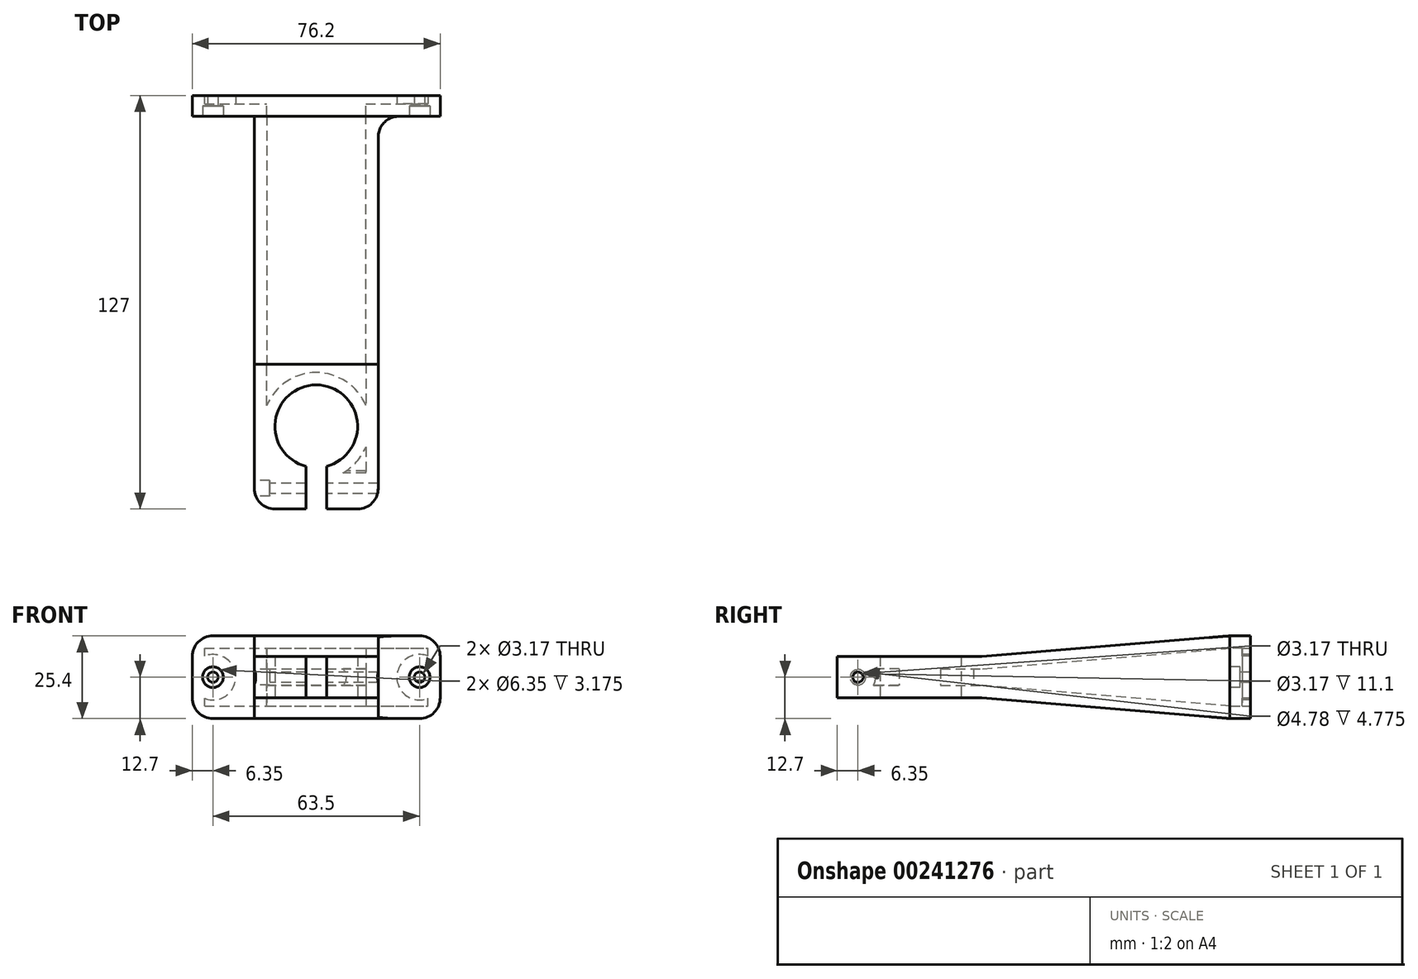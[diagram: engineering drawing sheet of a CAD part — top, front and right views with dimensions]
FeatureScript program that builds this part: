
annotation { "Feature Type Name" : "Feature", "Feature Type Description" : "" }
export const myFeature = defineFeature(function(context is Context, id is Id, definition is map)
    precondition{}
    {
        {
            var Q0;
            Q0=qCreatedBy(makeId("Front.planeOp"),FACE);
            var sketch = newSketch(context, id + "F0", { "sketchPlane" : qUnion([Q0])});
            skLineSegment(sketch, "E0.bottom", {"start": v(0, 0) * mm, "end": v(76.2, 0) * mm});
            skLineSegment(sketch, "E0.top", {"start": v(0, 25.4) * mm, "end": v(76.2, 25.4) * mm});
            skLineSegment(sketch, "E0.left", {"start": v(0, 0) * mm, "end": v(0, 25.4) * mm});
            skLineSegment(sketch, "E0.right", {"start": v(76.2, 0) * mm, "end": v(76.2, 25.4) * mm});
            skSolve(sketch);
        }
        {
            var Q0;
            Q0 = qSketchRegion(id + "F0", true);
            extrude(context, id + "F1", {"entities" : qUnion([Q0]), "depth" : 6.35 * mm});
        }
        {
            var Q0;
            Q0=makeQuery(id+"F1.opExtrude","CAP_FACE",FACE,{"disambiguationData":[OSD([sQuery(id+"F0.wireOp",EDGE,"E0.bottom"),sQuery(id+"F0.wireOp",EDGE,"E0.top"),sQuery(id+"F0.wireOp",EDGE,"E0.left"),sQuery(id+"F0.wireOp",EDGE,"E0.right")])],"isStart":false});
            var sketch = newSketch(context, id + "F2", { "sketchPlane" : qUnion([Q0])});
            skPoint(sketch, "E1", {"position": v(6.35, 12.7) * mm});
            skPoint(sketch, "E1.positionSnap0", {"position": v(0, 12.7) * mm});
            skPoint(sketch, "E2", {"position": v(69.85, 12.7) * mm});
            skSolve(sketch);
        }
        {
            var Q0;
            Q0=sQuery(id+"F2.wireOp",VERTEX,"E1");
            var Q1;
            Q1=sQuery(id+"F2.wireOp",VERTEX,"E2");
            var Q2;
            Q2=makeQuery(id+"F1.opExtrude","SWEPT_BODY",BODY,{"disambiguationData":[OSD([sQuery(id+"F0.wireOp",EDGE,"E0.bottom"),sQuery(id+"F0.wireOp",EDGE,"E0.top"),sQuery(id+"F0.wireOp",EDGE,"E0.left"),sQuery(id+"F0.wireOp",EDGE,"E0.right")])]});
            hole(context, id + "F3", {"style" : HoleStyle.C_BORE, "endStyle" : HoleEndStyle.THROUGH, "holeDiameter" : 3.17 * mm, "cBoreDiameter" : 6.35 * mm, "cBoreDepth" : 3.17 * mm, "tappedDepth" : 12.7 * mm, "tapClearance" : 3, "locations" : qUnion([Q0, Q1]), "scope" : qUnion([Q2])});
        }
        {
            var Q0;
            Q0=makeQuery(id+"F1.opExtrude","CAP_FACE",FACE,{"disambiguationData":[OSD([sQuery(id+"F0.wireOp",EDGE,"E0.bottom"),sQuery(id+"F0.wireOp",EDGE,"E0.top"),sQuery(id+"F0.wireOp",EDGE,"E0.left"),sQuery(id+"F0.wireOp",EDGE,"E0.right")])],"isStart":false});
            var sketch = newSketch(context, id + "F4", { "sketchPlane" : qUnion([Q0])});
            skLineSegment(sketch, "E3.bottom", {"start": v(19.05, 25.4) * mm, "end": v(57.15, 25.4) * mm});
            skLineSegment(sketch, "E3.top", {"start": v(19.05, 0) * mm, "end": v(57.15, 0) * mm});
            skLineSegment(sketch, "E3.left", {"start": v(19.05, 25.4) * mm, "end": v(19.05, 0) * mm});
            skLineSegment(sketch, "E3.right", {"start": v(57.15, 25.4) * mm, "end": v(57.15, 0) * mm});
            skSolve(sketch);
        }
        {
            var Q0;
            Q0=makeQuery(id+"F4.imprint","IMPRINT",FACE,{"disambiguationData":[TD([[makeQuery(id+"F4.imprint","IMPRINT",EDGE,{"derivedFrom":sQuery(id+"F4.wireOp",EDGE,"E3.bottom")}),-1.0]])]});
            cPlane(context, id + "F5", {"entities" : qUnion([Q0]), "cplaneType" : CPlaneType.OFFSET, "offset" : 76.2 * mm, "width" : 152.4 * mm, "height" : 152.4 * mm});
        }
        {
            var Q0;
            Q0=qCreatedBy(id+"F5.planeOp",FACE);
            var sketch = newSketch(context, id + "F6", { "sketchPlane" : qUnion([Q0])});
            skLineSegment(sketch, "E4.bottom", {"start": v(19.05, 6.35) * mm, "end": v(57.15, 6.35) * mm});
            skLineSegment(sketch, "E4.top", {"start": v(19.05, 19.05) * mm, "end": v(57.15, 19.05) * mm});
            skLineSegment(sketch, "E4.left", {"start": v(19.05, 6.35) * mm, "end": v(19.05, 19.05) * mm});
            skLineSegment(sketch, "E4.right", {"start": v(57.15, 6.35) * mm, "end": v(57.15, 19.05) * mm});
            skSolve(sketch);
        }
        {
            var Q1;
            Q1=makeQuery(id+"F4.imprint","IMPRINT",FACE,{"disambiguationData":[TD([[makeQuery(id+"F4.imprint","IMPRINT",EDGE,{"derivedFrom":sQuery(id+"F4.wireOp",EDGE,"E3.bottom")}),-1.0]])]});
            var Q2;
            Q2=makeQuery(id+"F6.imprint","IMPRINT",FACE,{"disambiguationData":[TD([[makeQuery(id+"F6.imprint","IMPRINT",EDGE,{"derivedFrom":sQuery(id+"F6.wireOp",EDGE,"E4.bottom")}),1.0]])]});
            loft(context, id + "F7", {"operationType" : NewBodyOperationType.ADD, "sheetProfilesArray" : [{ "sheetProfileEntities" : qUnion([Q1]) }, { "sheetProfileEntities" : qUnion([Q2]) }]});
        }
        {
            var Q0;
            Q0=makeQuery(id+"F7.opLoft","CAP_FACE",FACE,{"disambiguationData":[OSD([makeQuery(id+"F6.imprint","IMPRINT",FACE,{"disambiguationData":[TD([[makeQuery(id+"F6.imprint","IMPRINT",EDGE,{"derivedFrom":sQuery(id+"F6.wireOp",EDGE,"E4.bottom")}),1.0]])]})])],"isStart":true});
            extrude(context, id + "F8", {"entities" : qUnion([Q0]), "operationType" : NewBodyOperationType.ADD, "depth" : 44.45 * mm});
        }
        {
            var Q0;
            Q0=makeQuery(id+"F8.opExtrude","SWEPT_FACE",FACE,{"disambiguationData":[OSD([sQuery(id+"F6.wireOp",EDGE,"E4.bottom"),sQuery(id+"F6.wireOp",EDGE,"E4.left"),sQuery(id+"F6.wireOp",EDGE,"E4.right")])]});
            var sketch = newSketch(context, id + "F9", { "sketchPlane" : qUnion([Q0])});
            skArc(sketch, "E5", {"start": v(34.93, 113.9) * mm, "mid": v(38.1, 88.9) * mm, "end": v(41.28, 113.9) * mm});
            skPoint(sketch, "E5.centerSnap0", {"position": v(38.1, 127) * mm});
            skLineSegment(sketch, "E6", {"start": v(34.93, 127) * mm, "end": v(34.93, 113.9) * mm});
            skLineSegment(sketch, "E7", {"start": v(41.28, 127) * mm, "end": v(41.28, 113.9) * mm});
            skLineSegment(sketch, "E8", {"start": v(34.93, 127) * mm, "end": v(41.28, 127) * mm});
            skSolve(sketch);
        }
        {
            var Q0;
            Q0=makeQuery(id+"F9.imprint","IMPRINT",FACE,{"disambiguationData":[TD([[makeQuery(id+"F9.imprint","IMPRINT",EDGE,{"derivedFrom":sQuery(id+"F9.wireOp",EDGE,"E5")}),1.0]])]});
            extrude(context, id + "F10", {"entities" : qUnion([Q0]), "operationType" : NewBodyOperationType.REMOVE, "oppositeDirection" : true, "depth" : 25.4 * mm});
        }
        {
            var Q0;
            {var subQ0=sQuery(id+"F6.wireOp",EDGE,"E4.left");var subQ1=sQuery(id+"F6.wireOp",EDGE,"E4.top");var subQ2=sQuery(id+"F6.wireOp",EDGE,"E4.bottom");Q0=makeQuery(id+"F8.boolean.opBoolean","MERGE",FACE,{"derivedFrom":[makeQuery(id+"F7.opLoft","SWEPT_FACE",FACE,{"disambiguationData":[OSD([sQuery(id+"F0.wireOp",EDGE,"E0.bottom"),sQuery(id+"F0.wireOp",EDGE,"E0.top"),sQuery(id+"F4.wireOp",EDGE,"E3.bottom"),sQuery(id+"F4.wireOp",EDGE,"E3.top"),sQuery(id+"F4.wireOp",EDGE,"E3.left"),subQ2,subQ1,subQ0])]}),makeQuery(id+"F8.opExtrude","SWEPT_FACE",FACE,{"disambiguationData":[OSD([subQ2,subQ1,subQ0])]})]});}
            var sketch = newSketch(context, id + "F11", { "sketchPlane" : qUnion([Q0])});
            skPoint(sketch, "E9", {"position": v(120.65, 12.7) * mm});
            skPoint(sketch, "E9.positionSnap0", {"position": v(127, 12.7) * mm});
            skSolve(sketch);
        }
        {
            var Q0;
            Q0=sQuery(id+"F11.wireOp",VERTEX,"E9");
            var Q1;
            Q1=makeQuery(id+"F1.opExtrude","SWEPT_BODY",BODY,{"disambiguationData":[OSD([sQuery(id+"F0.wireOp",EDGE,"E0.bottom"),sQuery(id+"F0.wireOp",EDGE,"E0.top"),sQuery(id+"F0.wireOp",EDGE,"E0.left"),sQuery(id+"F0.wireOp",EDGE,"E0.right")])]});
            hole(context, id + "F12", {"style" : HoleStyle.C_BORE, "endStyle" : HoleEndStyle.THROUGH, "holeDiameter" : 3.17 * mm, "cBoreDiameter" : 4.78 * mm, "cBoreDepth" : 4.78 * mm, "tappedDepth" : 12.7 * mm, "tapClearance" : 3, "locations" : qUnion([Q0]), "scope" : qUnion([Q1])});
        }
        {
            var Q0;
            Q0=makeQuery(id+"F8.opExtrude","CAP_EDGE",EDGE,{"disambiguationData":[OSD([sQuery(id+"F6.wireOp",EDGE,"E4.bottom"),sQuery(id+"F6.wireOp",EDGE,"E4.top"),sQuery(id+"F6.wireOp",EDGE,"E4.left")])],"isStart":false});
            var Q1;
            Q1=makeQuery(id+"F8.opExtrude","CAP_EDGE",EDGE,{"disambiguationData":[OSD([sQuery(id+"F6.wireOp",EDGE,"E4.bottom"),sQuery(id+"F6.wireOp",EDGE,"E4.top"),sQuery(id+"F6.wireOp",EDGE,"E4.right")])],"isStart":false});
            fillet(context, id + "F13", {"entities" : qUnion([Q0, Q1]), "radius" : 6.35 * mm, "tangentPropagation" : true, "allowEdgeOverflow" : false});
        }
        {
            var Q0;
            Q0=makeQuery(id+"F1.opExtrude","CAP_FACE",FACE,{"disambiguationData":[OSD([sQuery(id+"F0.wireOp",EDGE,"E0.bottom"),sQuery(id+"F0.wireOp",EDGE,"E0.top"),sQuery(id+"F0.wireOp",EDGE,"E0.left"),sQuery(id+"F0.wireOp",EDGE,"E0.right")])],"isStart":true});
            shell(context, id + "F14", {"entities" : qUnion([Q0]), "thickness" : 3.8 * mm});
        }
        {
            var Q0;
            Q0=makeQuery(id+"F7.opLoft","MID_CAP_EDGE",EDGE,{"disambiguationData":[OSD([sQuery(id+"F0.wireOp",EDGE,"E0.bottom"),sQuery(id+"F0.wireOp",EDGE,"E0.top"),sQuery(id+"F4.wireOp",EDGE,"E3.bottom"),sQuery(id+"F4.wireOp",EDGE,"E3.top"),sQuery(id+"F4.wireOp",EDGE,"E3.left")])],"capPos":0.0});
            var Q1;
            Q1=makeQuery(id+"F7.opLoft","MID_CAP_EDGE",EDGE,{"disambiguationData":[OSD([sQuery(id+"F0.wireOp",EDGE,"E0.bottom"),sQuery(id+"F0.wireOp",EDGE,"E0.top"),sQuery(id+"F4.wireOp",EDGE,"E3.bottom"),sQuery(id+"F4.wireOp",EDGE,"E3.top"),sQuery(id+"F4.wireOp",EDGE,"E3.right")])],"capPos":0.0});
            var Q2;
            Q2=makeQuery(id+"F1.opExtrude","SWEPT_EDGE",EDGE,{"disambiguationData":[OSD([sQuery(id+"F0.wireOp",EDGE,"E0.top"),sQuery(id+"F0.wireOp",EDGE,"E0.right")])]});
            var Q3;
            Q3=makeQuery(id+"F1.opExtrude","SWEPT_EDGE",EDGE,{"disambiguationData":[OSD([sQuery(id+"F0.wireOp",EDGE,"E0.top"),sQuery(id+"F0.wireOp",EDGE,"E0.left")])]});
            var Q4;
            Q4=makeQuery(id+"F1.opExtrude","SWEPT_EDGE",EDGE,{"disambiguationData":[OSD([sQuery(id+"F0.wireOp",EDGE,"E0.bottom"),sQuery(id+"F0.wireOp",EDGE,"E0.left")])]});
            var Q5;
            Q5=makeQuery(id+"F1.opExtrude","SWEPT_EDGE",EDGE,{"disambiguationData":[OSD([sQuery(id+"F0.wireOp",EDGE,"E0.bottom"),sQuery(id+"F0.wireOp",EDGE,"E0.right")])]});
            fillet(context, id + "F15", {"entities" : qUnion([Q0, Q1, Q2, Q3, Q4, Q5]), "radius" : 6.35 * mm, "tangentPropagation" : true, "allowEdgeOverflow" : false});
        }
    });
